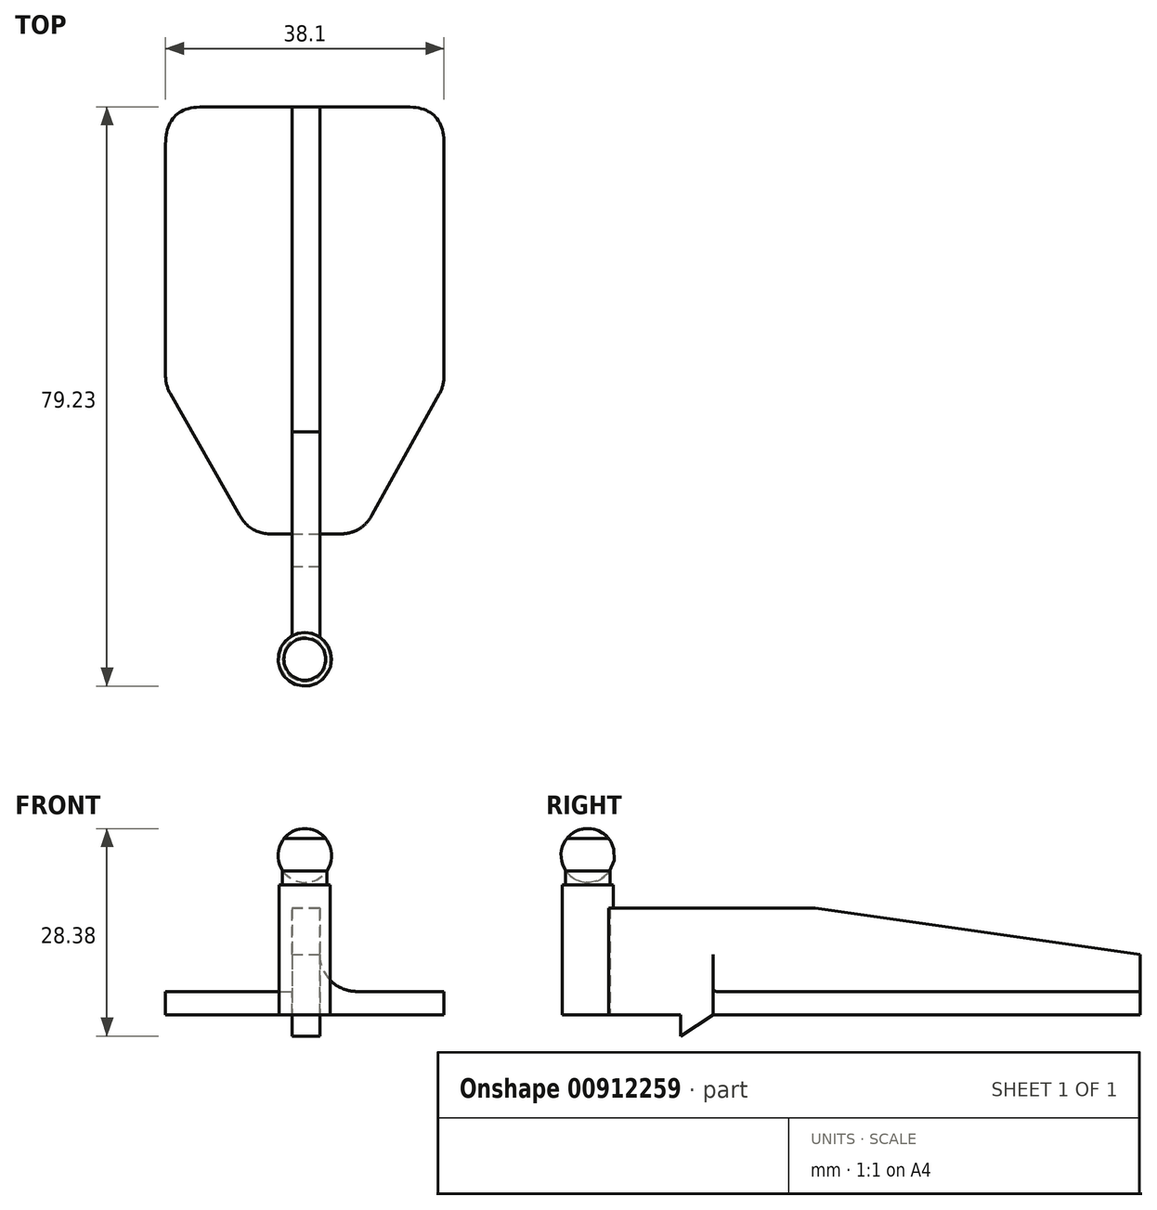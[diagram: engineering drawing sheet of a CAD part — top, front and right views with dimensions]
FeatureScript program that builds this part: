
annotation { "Feature Type Name" : "Feature", "Feature Type Description" : "" }
export const myFeature = defineFeature(function(context is Context, id is Id, definition is map)
    precondition{}
    {
        {
            var Q0;
            Q0=qCreatedBy(makeId("Top.planeOp"),FACE);
            var sketch = newSketch(context, id + "F0", { "sketchPlane" : qUnion([Q0])});
            skLineSegment(sketch, "E0", {"start": v(-7.48, -14.04) * mm, "end": v(7.76, -14.04) * mm});
            skLineSegment(sketch, "E1", {"start": v(0, -14.04) * mm, "end": v(0, 44.38) * mm});
            skPoint(sketch, "E1.startSnap0", {"position": v(0.14, -14.04) * mm});
            skLineSegment(sketch, "E2", {"start": v(-19.05, 44.38) * mm, "end": v(19.05, 44.38) * mm});
            skLineSegment(sketch, "E3", {"start": v(19.05, 44.38) * mm, "end": v(19.05, 6.28) * mm});
            skLineSegment(sketch, "E4", {"start": v(-19.05, 44.38) * mm, "end": v(-19.05, 6.28) * mm});
            skLineSegment(sketch, "E5", {"start": v(-19.05, 6.28) * mm, "end": v(-7.48, -14.04) * mm});
            skLineSegment(sketch, "E6", {"start": v(19.05, 6.28) * mm, "end": v(7.76, -14.04) * mm});
            skSolve(sketch);
        }
        {
            var Q0;
            Q0 = qSketchRegion(id + "F0", true);
            extrude(context, id + "F1", {"entities" : qUnion([Q0]), "depth" : 3.17 * mm, "offsetDistance" : 25.4 * mm});
        }
        {
            var Q0;
            Q0=makeQuery(id+"F1.opExtrude","CAP_FACE",FACE,{"disambiguationData":[OSD([sQuery(id+"F0.wireOp",EDGE,"E0"),sQuery(id+"F0.wireOp",EDGE,"E2"),sQuery(id+"F0.wireOp",EDGE,"E3"),sQuery(id+"F0.wireOp",EDGE,"E4"),sQuery(id+"F0.wireOp",EDGE,"E5"),sQuery(id+"F0.wireOp",EDGE,"E6")])],"isStart":false});
            var sketch = newSketch(context, id + "F2", { "sketchPlane" : qUnion([Q0])});
            skLineSegment(sketch, "E7", {"start": v(0, 0) * mm, "end": v(0.14, -14.04) * mm});
            skLineSegment(sketch, "E8", {"start": v(0.14, -14.04) * mm, "end": v(0.14, 44.38) * mm});
            skLineSegment(sketch, "E9", {"start": v(0.14, 44.38) * mm, "end": v(-1.76, 44.38) * mm});
            skLineSegment(sketch, "E10", {"start": v(-1.76, 44.38) * mm, "end": v(2.05, 44.38) * mm});
            skLineSegment(sketch, "E11", {"start": v(2.05, 44.38) * mm, "end": v(2.05, -28.36) * mm});
            skCircle(sketch, "E12", {"center": v(0, -31.19) * mm, "radius": 3.5 * mm});
            skLineSegment(sketch, "E13", {"start": v(-1.76, 44.38) * mm, "end": v(-1.76, -28.17) * mm});
            skSolve(sketch);
        }
        {
            var Q0;
            {var subQ0=sQuery(id+"F2.wireOp",EDGE,"E8");Q0=makeQuery(id+"F2.imprint","IMPRINT",FACE,{"disambiguationData":[TD([[makeQuery(id+"F2.imprint","IMPRINT",EDGE,{"derivedFrom":subQ0}),1.0]])]});}
            var Q1;
            {var subQ0=sQuery(id+"F2.wireOp",EDGE,"E8");Q1=makeQuery(id+"F2.imprint","IMPRINT",FACE,{"disambiguationData":[TD([[makeQuery(id+"F2.imprint","IMPRINT",EDGE,{"derivedFrom":subQ0}),-1.0]])]});}
            var Q2;
            {var subQ2=sQuery(id+"F2.wireOp",EDGE,"E11");var subQ5=sQuery(id+"F2.wireOp",EDGE,"E12");var subQ8=makeQuery(id+"F2.imprint","INTERSECT",VERTEX,{"derivedFrom":[subQ2,subQ5]});Q2=makeQuery(id+"F2.imprint","IMPRINT",FACE,{"disambiguationData":[TD([[makeQuery(id+"F2.imprint","IMPRINT",EDGE,{"disambiguationData":[TD([[subQ8,1.0]])],"derivedFrom":subQ2}),-1.0]])]});}
            extrude(context, id + "F3", {"entities" : qUnion([Q0, Q1, Q2]), "operationType" : NewBodyOperationType.ADD, "depth" : 11.43 * mm, "offsetDistance" : 25.4 * mm});
        }
        {
            var Q0;
            {var subQ0=sQuery(id+"F2.wireOp",EDGE,"E12");var subQ1=makeQuery(id+"F2.imprint","INTERSECT",VERTEX,{"derivedFrom":[sQuery(id+"F2.wireOp",EDGE,"E11"),subQ0]});Q0=makeQuery(id+"F2.imprint","IMPRINT",FACE,{"disambiguationData":[TD([[makeQuery(id+"F2.imprint","IMPRINT",EDGE,{"disambiguationData":[TD([[subQ1,-1.0]])],"derivedFrom":subQ0}),1.0]])]});}
            extrude(context, id + "F4", {"entities" : qUnion([Q0]), "operationType" : NewBodyOperationType.ADD, "depth" : 20.95 * mm, "offsetDistance" : 25.4 * mm});
        }
        {
            var Q0;
            Q0 = qSketchRegion(id + "F2", true);
            extrude(context, id + "F5", {"entities" : qUnion([Q0]), "operationType" : NewBodyOperationType.ADD, "oppositeDirection" : true, "depth" : 3.17 * mm, "offsetDistance" : 25.4 * mm});
        }
        {
            var Q0;
            {var subQ0=sQuery(id+"F2.wireOp",EDGE,"E11");Q0=makeQuery(id+"F5.boolean.opBoolean","MERGE",FACE,{"derivedFrom":[makeQuery(id+"F3.opExtrude","SWEPT_FACE",FACE,{"disambiguationData":[OSD([subQ0])]}),makeQuery(id+"F5.opExtrude","SWEPT_FACE",FACE,{"disambiguationData":[OSD([subQ0])]})]});}
            var sketch = newSketch(context, id + "F6", { "sketchPlane" : qUnion([Q0])});
            skLineSegment(sketch, "E14", {"start": v(44.38, 14.6) * mm, "end": v(-0.07, 14.6) * mm});
            skLineSegment(sketch, "E15", {"start": v(44.38, 3.18) * mm, "end": v(44.38, 8.26) * mm});
            skLineSegment(sketch, "E16", {"start": v(44.38, 8.26) * mm, "end": v(44.38, 14.6) * mm});
            skLineSegment(sketch, "E17", {"start": v(44.38, 8.26) * mm, "end": v(-0.07, 14.6) * mm});
            skLineSegment(sketch, "E18", {"start": v(-14.04, 0) * mm, "end": v(-18.49, 0) * mm});
            skLineSegment(sketch, "E19", {"start": v(-18.49, 0) * mm, "end": v(-18.49, -2.92) * mm});
            skLineSegment(sketch, "E20", {"start": v(-18.49, -2.92) * mm, "end": v(-14.04, 0) * mm});
            skSolve(sketch);
        }
        {
            var Q0;
            Q0=makeQuery(id+"F6.imprint","IMPRINT",FACE,{"disambiguationData":[TD([[makeQuery(id+"F6.imprint","IMPRINT",EDGE,{"derivedFrom":sQuery(id+"F6.wireOp",EDGE,"E14")}),1.0]])]});
            extrude(context, id + "F7", {"entities" : qUnion([Q0]), "operationType" : NewBodyOperationType.REMOVE, "oppositeDirection" : true, "depth" : 25.4 * mm, "offsetDistance" : 25.4 * mm});
        }
        {
            var Q0;
            Q0=makeQuery(id+"F6.imprint","IMPRINT",FACE,{"disambiguationData":[TD([[makeQuery(id+"F6.imprint","IMPRINT",EDGE,{"derivedFrom":sQuery(id+"F6.wireOp",EDGE,"E18")}),1.0]])]});
            extrude(context, id + "F8", {"entities" : qUnion([Q0]), "operationType" : NewBodyOperationType.ADD, "oppositeDirection" : true, "depth" : 3.8 * mm, "offsetDistance" : 25.4 * mm});
        }
        {
            var Q0;
            Q0=makeQuery(id+"F4.opExtrude","CAP_FACE",FACE,{"disambiguationData":[OSD([sQuery(id+"F2.wireOp",EDGE,"E12")])],"isStart":false});
            extrude(context, id + "F9", {"entities" : qUnion([Q0]), "operationType" : NewBodyOperationType.REMOVE, "oppositeDirection" : true, "depth" : 6.35 * mm, "offsetDistance" : 25.4 * mm});
        }
        {
            var Q0;
            Q0=makeQuery(id+"F9.boolean.opBoolean","COPY",FACE,{"derivedFrom":makeQuery(id+"F9.opExtrude","CAP_FACE",FACE,{"disambiguationData":[OSD([sQuery(id+"F2.wireOp",EDGE,"E12")])],"isStart":false})});
            var sketch = newSketch(context, id + "F10", { "sketchPlane" : qUnion([Q0])});
            skLineSegment(sketch, "E21.bottom", {"start": v(0, -31.19) * mm, "end": v(0.5, -31.19) * mm});
            skLineSegment(sketch, "E21.top", {"start": v(0, -30.68) * mm, "end": v(0.5, -30.68) * mm});
            skLineSegment(sketch, "E21.left", {"start": v(0, -31.19) * mm, "end": v(0, -30.68) * mm});
            skLineSegment(sketch, "E21.right", {"start": v(0.5, -31.19) * mm, "end": v(0.5, -30.68) * mm});
            skLineSegment(sketch, "E22.bottom", {"start": v(0.5, -30.68) * mm, "end": v(-0.5, -30.68) * mm});
            skLineSegment(sketch, "E22.top", {"start": v(0.5, -31.7) * mm, "end": v(-0.5, -31.7) * mm});
            skLineSegment(sketch, "E22.left", {"start": v(0.5, -30.68) * mm, "end": v(0.5, -31.7) * mm});
            skLineSegment(sketch, "E22.right", {"start": v(-0.5, -30.68) * mm, "end": v(-0.5, -31.7) * mm});
            skSolve(sketch);
        }
        {
            var Q0;
            {var subQ0=sQuery(id+"F10.wireOp",EDGE,"E21.bottom");Q0=makeQuery(id+"F10.imprint","IMPRINT",FACE,{"disambiguationData":[TD([[makeQuery(id+"F10.imprint","IMPRINT",EDGE,{"derivedFrom":subQ0}),1.0]])]});}
            extrude(context, id + "F11", {"entities" : qUnion([Q0]), "operationType" : NewBodyOperationType.ADD, "depth" : 6.35 * mm, "offsetDistance" : 25.4 * mm});
        }
        {
            var Q0;
            Q0=makeQuery(id+"F11.opExtrude","SWEPT_FACE",FACE,{"disambiguationData":[OSD([sQuery(id+"F10.wireOp",EDGE,"E21.left")])]});
            var sketch = newSketch(context, id + "F12", { "sketchPlane" : qUnion([Q0])});
            skLineSegment(sketch, "E23", {"start": v(31.19, 17.78) * mm, "end": v(31.19, 24.13) * mm});
            skLineSegment(sketch, "E24", {"start": v(31.19, 24.13) * mm, "end": v(34.05, 24.13) * mm});
            skLineSegment(sketch, "E25", {"start": v(31.19, 17.78) * mm, "end": v(34.24, 17.78) * mm});
            skLineSegment(sketch, "E26", {"start": v(34.24, 17.78) * mm, "end": v(34.24, 19.69) * mm});
            skArc(sketch, "E27", {"start": v(34.24, 19.69) * mm, "mid": v(34.89, 21.94) * mm, "end": v(34.05, 24.13) * mm});
            skSolve(sketch);
        }
        {
            var Q0;
            Q0=makeQuery(id+"F12.imprint","IMPRINT",FACE,{"disambiguationData":[TD([[makeQuery(id+"F12.imprint","IMPRINT",EDGE,{"derivedFrom":sQuery(id+"F12.wireOp",EDGE,"E23")}),1.0]])]});
            var Q1;
            Q1=sQuery(id+"F12.wireOp",EDGE,"E23");
            revolve(context, id + "F13", {"operationType" : NewBodyOperationType.ADD, "surfaceOperationType" : NewSurfaceOperationType.NEW, "entities" : qUnion([Q0]), "axis" : qUnion([Q1]), "revolveType" : RevolveType.FULL});
        }
        {
            var Q0;
            Q0=makeQuery(id+"F7.boolean.opBoolean","COPY",EDGE,{"derivedFrom":makeQuery(id+"F7.opExtrude","SWEPT_EDGE",EDGE,{"disambiguationData":[OSD([sQuery(id+"F6.wireOp",EDGE,"E15"),sQuery(id+"F6.wireOp",EDGE,"E16"),sQuery(id+"F6.wireOp",EDGE,"E17")])]})});
            var Q1;
            Q1=makeQuery(id+"F7.boolean.opBoolean","COPY",EDGE,{"derivedFrom":makeQuery(id+"F7.opExtrude","SWEPT_EDGE",EDGE,{"disambiguationData":[OSD([sQuery(id+"F2.wireOp",EDGE,"E11"),sQuery(id+"F6.wireOp",EDGE,"E14"),sQuery(id+"F6.wireOp",EDGE,"E17")])]})});
            var Q2;
            Q2=makeQuery(id+"F1.opExtrude","SWEPT_EDGE",EDGE,{"disambiguationData":[OSD([sQuery(id+"F0.wireOp",EDGE,"E2"),sQuery(id+"F0.wireOp",EDGE,"E3")])]});
            var Q3;
            Q3=makeQuery(id+"F1.opExtrude","SWEPT_EDGE",EDGE,{"disambiguationData":[OSD([sQuery(id+"F0.wireOp",EDGE,"E3"),sQuery(id+"F0.wireOp",EDGE,"E6")])]});
            var Q4;
            Q4=makeQuery(id+"F1.opExtrude","SWEPT_EDGE",EDGE,{"disambiguationData":[OSD([sQuery(id+"F0.wireOp",EDGE,"E0"),sQuery(id+"F0.wireOp",EDGE,"E6")])]});
            var Q5;
            Q5=makeQuery(id+"F1.opExtrude","SWEPT_EDGE",EDGE,{"disambiguationData":[OSD([sQuery(id+"F0.wireOp",EDGE,"E2"),sQuery(id+"F0.wireOp",EDGE,"E4")])]});
            var Q6;
            Q6=makeQuery(id+"F1.opExtrude","SWEPT_EDGE",EDGE,{"disambiguationData":[OSD([sQuery(id+"F0.wireOp",EDGE,"E4"),sQuery(id+"F0.wireOp",EDGE,"E5")])]});
            var Q7;
            Q7=makeQuery(id+"F1.opExtrude","SWEPT_EDGE",EDGE,{"disambiguationData":[OSD([sQuery(id+"F0.wireOp",EDGE,"E0"),sQuery(id+"F0.wireOp",EDGE,"E5")])]});
            fillet(context, id + "F14", {"entities" : qUnion([Q0, Q1, Q2, Q3, Q4, Q5, Q6, Q7]), "radius" : 5.08 * mm, "tangentPropagation" : true, "rho" : 0.5, "crossSection" : FilletCrossSection.CONIC, "allowEdgeOverflow" : false});
        }
        {
            var Q0;
            {var subQ0=sQuery(id+"F2.wireOp",EDGE,"E13");Q0=makeQuery(id+"F3.boolean.opBoolean","SPLIT",EDGE,{"disambiguationData":[topologyDisambiguationEdgeConnected([makeQuery(id+"F1.opExtrude","CAP_FACE",FACE,{"disambiguationData":[OSD([sQuery(id+"F0.wireOp",EDGE,"E0"),sQuery(id+"F0.wireOp",EDGE,"E2"),sQuery(id+"F0.wireOp",EDGE,"E3"),sQuery(id+"F0.wireOp",EDGE,"E4"),sQuery(id+"F0.wireOp",EDGE,"E5"),sQuery(id+"F0.wireOp",EDGE,"E6")])],"isStart":false})])],"derivedFrom":makeQuery(id+"F3.opExtrude","CAP_EDGE",EDGE,{"disambiguationData":[OSD([subQ0])],"isStart":true})});}
            var Q1;
            {var subQ0=sQuery(id+"F2.wireOp",EDGE,"E11");Q1=makeQuery(id+"F3.boolean.opBoolean","SPLIT",EDGE,{"disambiguationData":[topologyDisambiguationEdgeConnected([makeQuery(id+"F1.opExtrude","CAP_FACE",FACE,{"disambiguationData":[OSD([sQuery(id+"F0.wireOp",EDGE,"E0"),sQuery(id+"F0.wireOp",EDGE,"E2"),sQuery(id+"F0.wireOp",EDGE,"E3"),sQuery(id+"F0.wireOp",EDGE,"E4"),sQuery(id+"F0.wireOp",EDGE,"E5"),sQuery(id+"F0.wireOp",EDGE,"E6")])],"isStart":false})])],"derivedFrom":makeQuery(id+"F3.opExtrude","CAP_EDGE",EDGE,{"disambiguationData":[OSD([subQ0])],"isStart":true})});}
            fillet(context, id + "F15", {"entities" : qUnion([Q0, Q1]), "radius" : 5.08 * mm, "tangentPropagation" : true, "allowEdgeOverflow" : false});
        }
    });
